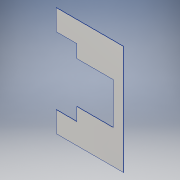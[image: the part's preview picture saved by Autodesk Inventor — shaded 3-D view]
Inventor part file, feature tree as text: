
AUTODESK INVENTOR PART (.ipt)
format: ipt  version: 2016 (Build 200138000, 138)  size: 104,448 bytes
history: native  units: in
note: dims shown in document units (in); Inventor stores cm internally (conversion verified against a paired STEP export)
features: extrude x1, sketch x1
ambient origin geometry x8: Origin, YZ Plane, XZ Plane, XY Plane, X Axis, Y Axis, Z Axis, Center Point
bodies: Solid1 (feature_tree)
feature tree (2):
  extrude  "Extrusion1"  Depth=13.0in
  sketch  "Sketch1"  dims[d2=0.0625in d3=0.0in d4=13.0in d5=4.0in d6=4.0in d7=17.0in d9=2.5in d10=2.5in d11=2.0in d12=4.0in]
